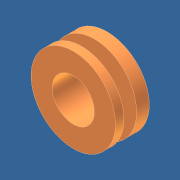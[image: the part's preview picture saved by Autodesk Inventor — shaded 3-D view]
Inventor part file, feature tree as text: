
AUTODESK INVENTOR PART (.ipt)
format: ipt  version: unknown  size: 190,976 bytes
history: native  units: in
note: dims shown in document units (in); Inventor stores cm internally (conversion verified against a paired STEP export)
features: extrude x4, sketch x4, projected_geometry x1
ambient origin geometry x8: Origin, YZ Plane, XZ Plane, XY Plane, X Axis, Y Axis, Z Axis, Center Point
bodies: Solid1 (feature_tree)
feature tree (9):
  extrude  "Extrusion1"  Depth=0.075in TaperAngle=0.0deg
  extrude  "Extrusion2"  Depth=0.075in TaperAngle=0.0deg
  extrude  "Extrusion3"  Depth=0.25in
  extrude  "Extrusion4"  [1 undecoded]
  sketch  "Sketch1"  dims[d0=0.5in d1=0.075in d2=0.0in]
  sketch  "Sketch2"  dims[d3=0.275in d4=0.075in d5=0.0in]
  sketch  "Sketch3"  dims[d6=0.05in d7=0.0in d8=0.25in]
  projected_geometry  "Projected Loop1"
  sketch  "Sketch4"  dims[d9=0.05in d10=0.0in]
note: 1 required parameter value undecoded (feature->parameter linkage not recoverable at this tier; creation-order binding heuristic only, values carry confidence <= 0.55)
